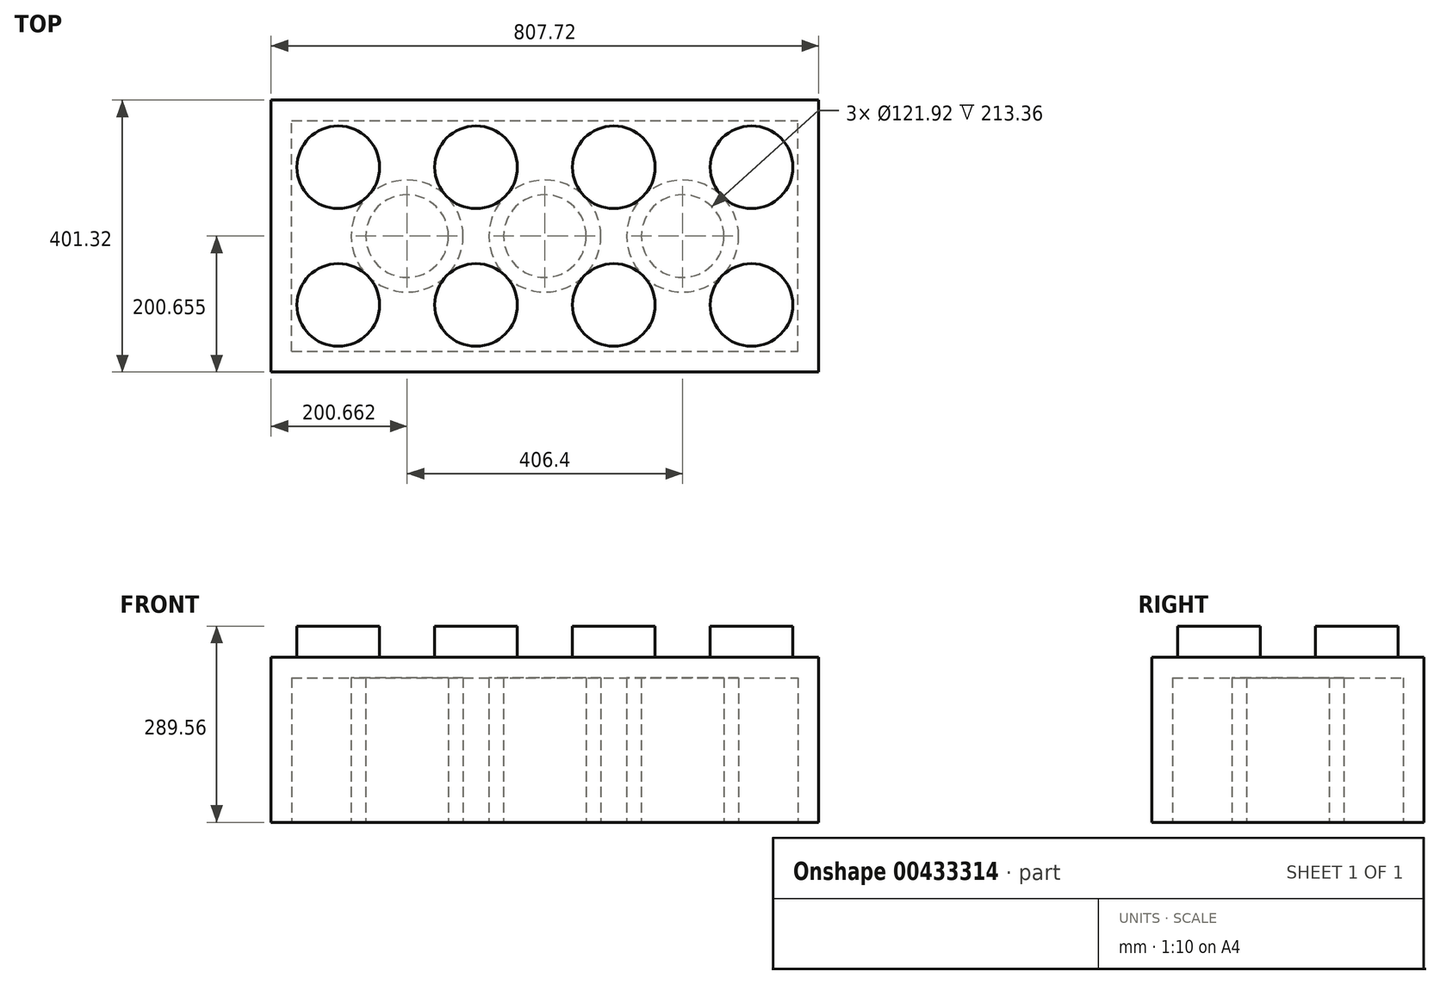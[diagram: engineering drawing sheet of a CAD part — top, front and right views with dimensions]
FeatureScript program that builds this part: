
annotation { "Feature Type Name" : "Feature", "Feature Type Description" : "" }
export const myFeature = defineFeature(function(context is Context, id is Id, definition is map)
    precondition{}
    {
        {
            var Q0;
            Q0=qCreatedBy(makeId("Top.planeOp"),FACE);
            var sketch = newSketch(context, id + "F0", { "sketchPlane" : qUnion([Q0])});
            skLineSegment(sketch, "E0.bottom", {"start": v(-395.75, 199.93) * mm, "end": v(411.97, 199.93) * mm});
            skLineSegment(sketch, "E0.top", {"start": v(-395.75, -201.4) * mm, "end": v(411.97, -201.4) * mm});
            skLineSegment(sketch, "E0.left", {"start": v(-395.75, 199.93) * mm, "end": v(-395.75, -201.4) * mm});
            skLineSegment(sketch, "E0.right", {"start": v(411.97, 199.93) * mm, "end": v(411.97, -201.4) * mm});
            skSolve(sketch);
        }
        {
            var Q0;
            Q0=makeQuery(id+"F0.imprint","IMPRINT",FACE,{"disambiguationData":[TD([[makeQuery(id+"F0.imprint","IMPRINT",EDGE,{"derivedFrom":sQuery(id+"F0.wireOp",EDGE,"E0.bottom")}),-1.0]])]});
            extrude(context, id + "F1", {"entities" : qUnion([Q0]), "depth" : 243.84 * mm});
        }
        {
            var Q0;
            Q0=makeQuery(id+"F1.opExtrude","CAP_FACE",FACE,{"disambiguationData":[OSD([sQuery(id+"F0.wireOp",EDGE,"E0.bottom"),sQuery(id+"F0.wireOp",EDGE,"E0.top"),sQuery(id+"F0.wireOp",EDGE,"E0.left"),sQuery(id+"F0.wireOp",EDGE,"E0.right")])],"isStart":false});
            var sketch = newSketch(context, id + "F2", { "sketchPlane" : qUnion([Q0])});
            skCircle(sketch, "E1", {"center": v(-296.69, 100.87) * mm, "radius": 60.96 * mm});
            skCircle(sketch, "E2.0.1.0", {"center": v(-296.69, -102.33) * mm, "radius": 60.96 * mm});
            skCircle(sketch, "E2.1.0.0", {"center": v(-93.49, 100.87) * mm, "radius": 60.96 * mm});
            skCircle(sketch, "E2.1.1.0", {"center": v(-93.49, -102.33) * mm, "radius": 60.96 * mm});
            skCircle(sketch, "E2.2.0.0", {"center": v(109.71, 100.87) * mm, "radius": 60.96 * mm});
            skCircle(sketch, "E2.2.1.0", {"center": v(109.71, -102.33) * mm, "radius": 60.96 * mm});
            skCircle(sketch, "E2.3.0.0", {"center": v(312.91, 100.87) * mm, "radius": 60.96 * mm});
            skCircle(sketch, "E2.3.1.0", {"center": v(312.91, -102.33) * mm, "radius": 60.96 * mm});
            skLineSegment(sketch, "E2.direction1", {"start": v(-296.69, 100.87) * mm, "end": v(-93.49, 100.87) * mm, "construction": true});
            skLineSegment(sketch, "E2.direction2", {"start": v(-296.69, 100.87) * mm, "end": v(-296.69, -102.33) * mm, "construction": true});
            skSolve(sketch);
        }
        {
            var Q0;
            Q0=makeQuery(id+"F2.imprint","IMPRINT",FACE,{"disambiguationData":[TD([[makeQuery(id+"F2.imprint","IMPRINT",EDGE,{"derivedFrom":sQuery(id+"F2.wireOp",EDGE,"E1")}),1.0]])]});
            var Q1;
            Q1=makeQuery(id+"F2.imprint","IMPRINT",FACE,{"disambiguationData":[TD([[makeQuery(id+"F2.imprint","IMPRINT",EDGE,{"derivedFrom":sQuery(id+"F2.wireOp",EDGE,"E2.0.1.0")}),1.0]])]});
            var Q2;
            Q2=makeQuery(id+"F2.imprint","IMPRINT",FACE,{"disambiguationData":[TD([[makeQuery(id+"F2.imprint","IMPRINT",EDGE,{"derivedFrom":sQuery(id+"F2.wireOp",EDGE,"E2.1.1.0")}),1.0]])]});
            var Q3;
            Q3=makeQuery(id+"F2.imprint","IMPRINT",FACE,{"disambiguationData":[TD([[makeQuery(id+"F2.imprint","IMPRINT",EDGE,{"derivedFrom":sQuery(id+"F2.wireOp",EDGE,"E2.1.0.0")}),1.0]])]});
            var Q4;
            Q4=makeQuery(id+"F2.imprint","IMPRINT",FACE,{"disambiguationData":[TD([[makeQuery(id+"F2.imprint","IMPRINT",EDGE,{"derivedFrom":sQuery(id+"F2.wireOp",EDGE,"E2.2.0.0")}),1.0]])]});
            var Q5;
            Q5=makeQuery(id+"F2.imprint","IMPRINT",FACE,{"disambiguationData":[TD([[makeQuery(id+"F2.imprint","IMPRINT",EDGE,{"derivedFrom":sQuery(id+"F2.wireOp",EDGE,"E2.2.1.0")}),1.0]])]});
            var Q6;
            Q6=makeQuery(id+"F2.imprint","IMPRINT",FACE,{"disambiguationData":[TD([[makeQuery(id+"F2.imprint","IMPRINT",EDGE,{"derivedFrom":sQuery(id+"F2.wireOp",EDGE,"E2.3.1.0")}),1.0]])]});
            var Q7;
            Q7=makeQuery(id+"F2.imprint","IMPRINT",FACE,{"disambiguationData":[TD([[makeQuery(id+"F2.imprint","IMPRINT",EDGE,{"derivedFrom":sQuery(id+"F2.wireOp",EDGE,"E2.3.0.0")}),1.0]])]});
            extrude(context, id + "F3", {"entities" : qUnion([Q0, Q1, Q2, Q3, Q4, Q5, Q6, Q7]), "operationType" : NewBodyOperationType.ADD, "depth" : 45.72 * mm});
        }
        {
            var Q0;
            Q0=makeQuery(id+"F0.imprint","IMPRINT",FACE,{"disambiguationData":[TD([[makeQuery(id+"F0.imprint","IMPRINT",EDGE,{"derivedFrom":sQuery(id+"F0.wireOp",EDGE,"E0.bottom")}),-1.0]])]});
            var sketch = newSketch(context, id + "F4", { "sketchPlane" : qUnion([Q0])});
            skLineSegment(sketch, "E3.bottom", {"start": v(-365.27, -170.91) * mm, "end": v(381.5, -170.91) * mm});
            skLineSegment(sketch, "E3.top", {"start": v(-365.27, 169.45) * mm, "end": v(381.5, 169.45) * mm});
            skLineSegment(sketch, "E3.left", {"start": v(-365.27, -170.91) * mm, "end": v(-365.27, 169.45) * mm});
            skLineSegment(sketch, "E3.right", {"start": v(381.5, -170.91) * mm, "end": v(381.5, 169.45) * mm});
            skSolve(sketch);
        }
        {
            var Q0;
            Q0 = qSketchRegion(id + "F4", true);
            extrude(context, id + "F5", {"entities" : qUnion([Q0]), "operationType" : NewBodyOperationType.REMOVE, "depth" : 213.36 * mm});
        }
        {
            var Q0;
            Q0=makeQuery(id+"F0.imprint","IMPRINT",FACE,{"disambiguationData":[TD([[makeQuery(id+"F0.imprint","IMPRINT",EDGE,{"derivedFrom":sQuery(id+"F0.wireOp",EDGE,"E0.bottom")}),-1.0]])]});
            var sketch = newSketch(context, id + "F6", { "sketchPlane" : qUnion([Q0])});
            skCircle(sketch, "E4", {"center": v(211.31, -0.73) * mm, "radius": 60.96 * mm});
            skCircle(sketch, "E5", {"center": v(211.31, -0.73) * mm, "radius": 82.55 * mm});
            skCircle(sketch, "E6.1.0.0", {"center": v(8.11, -0.73) * mm, "radius": 82.55 * mm});
            skCircle(sketch, "E6.1.0.1", {"center": v(8.11, -0.73) * mm, "radius": 60.96 * mm});
            skCircle(sketch, "E6.2.0.0", {"center": v(-195.09, -0.73) * mm, "radius": 82.55 * mm});
            skCircle(sketch, "E6.2.0.1", {"center": v(-195.09, -0.73) * mm, "radius": 60.96 * mm});
            skLineSegment(sketch, "E6.direction1", {"start": v(211.31, -0.73) * mm, "end": v(8.11, -0.73) * mm, "construction": true});
            skSolve(sketch);
        }
        {
            var Q0;
            Q0 = qSketchRegion(id + "F6", true);
            extrude(context, id + "F7", {"entities" : qUnion([Q0]), "operationType" : NewBodyOperationType.REMOVE, "depth" : 142.24 * mm});
        }
        {
            var Q0;
            Q0 = qSketchRegion(id + "F6", true);
            extrude(context, id + "F8", {"entities" : qUnion([Q0]), "operationType" : NewBodyOperationType.ADD, "depth" : 213.36 * mm});
        }
    });
